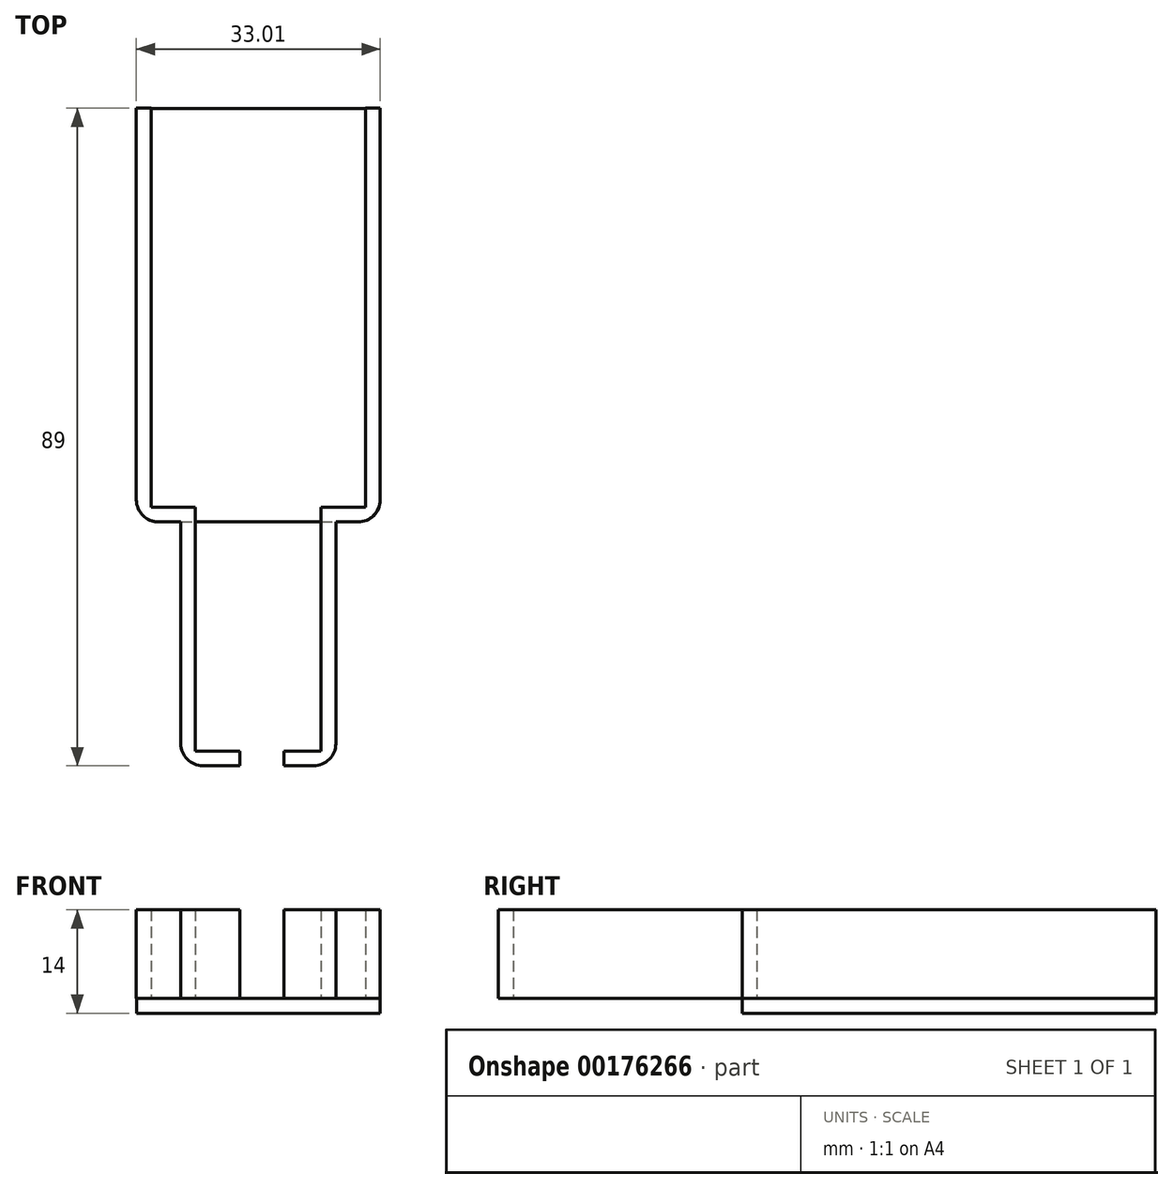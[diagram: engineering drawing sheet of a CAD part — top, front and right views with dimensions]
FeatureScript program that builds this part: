
annotation { "Feature Type Name" : "Feature", "Feature Type Description" : "" }
export const myFeature = defineFeature(function(context is Context, id is Id, definition is map)
    precondition{}
    {
        {
            var Q0;
            Q0=qCreatedBy(makeId("Top.planeOp"),FACE);
            var sketch = newSketch(context, id + "F0", { "sketchPlane" : qUnion([Q0])});
            skLineSegment(sketch, "E0.left", {"start": v(-20.44, 45.13) * mm, "end": v(-20.44, -8.87) * mm});
            skLineSegment(sketch, "E0.right", {"start": v(10.56, 45.13) * mm, "end": v(10.56, -8.87) * mm});
            skLineSegment(sketch, "E1.top", {"start": v(-14.44, -43.87) * mm, "end": v(-6.44, -43.87) * mm});
            skLineSegment(sketch, "E1.left", {"start": v(-14.44, -10.87) * mm, "end": v(-14.44, -43.87) * mm});
            skLineSegment(sketch, "E1.right", {"start": v(6.56, -10.87) * mm, "end": v(6.56, -43.87) * mm});
            skLineSegment(sketch, "E2", {"start": v(-6.44, -43.87) * mm, "end": v(-6.44, -43.87) * mm});
            skLineSegment(sketch, "E3", {"start": v(-0.44, -43.87) * mm, "end": v(-0.44, -43.87) * mm});
            skLineSegment(sketch, "E4.trimOffspring", {"start": v(-0.44, -43.87) * mm, "end": v(6.56, -43.87) * mm});
            skLineSegment(sketch, "E5.0", {"start": v(-0.44, -41.87) * mm, "end": v(4.56, -41.87) * mm});
            skLineSegment(sketch, "E6.0", {"start": v(4.56, -8.87) * mm, "end": v(4.56, -41.87) * mm});
            skLineSegment(sketch, "E7.0", {"start": v(-12.44, -8.87) * mm, "end": v(-12.44, -41.87) * mm});
            skLineSegment(sketch, "E8.0", {"start": v(-12.44, -41.87) * mm, "end": v(-6.44, -41.87) * mm});
            skLineSegment(sketch, "E9.0", {"start": v(12.56, 45.13) * mm, "end": v(12.56, -8.87) * mm});
            skLineSegment(sketch, "E10", {"start": v(-6.44, -41.87) * mm, "end": v(-6.44, -43.87) * mm});
            skLineSegment(sketch, "E11", {"start": v(-0.44, -41.87) * mm, "end": v(-0.44, -43.87) * mm});
            skLineSegment(sketch, "E12", {"start": v(-20.44, 45.13) * mm, "end": v(-18.44, 45.13) * mm});
            skLineSegment(sketch, "E13", {"start": v(-20.44, -8.87) * mm, "end": v(-20.44, -10.87) * mm});
            skLineSegment(sketch, "E14", {"start": v(-20.44, -10.87) * mm, "end": v(-14.44, -10.87) * mm});
            skPoint(sketch, "E15.end.orphan", {"position": v(-18.44, -8.87) * mm});
            skLineSegment(sketch, "E16", {"start": v(-18.44, 45.13) * mm, "end": v(-18.44, -8.87) * mm});
            skLineSegment(sketch, "E17", {"start": v(12.56, -8.87) * mm, "end": v(12.56, -10.87) * mm});
            skLineSegment(sketch, "E18", {"start": v(12.56, -10.87) * mm, "end": v(6.56, -10.87) * mm});
            skLineSegment(sketch, "E19", {"start": v(-12.44, -8.87) * mm, "end": v(-18.44, -8.87) * mm});
            skLineSegment(sketch, "E20", {"start": v(4.56, -8.87) * mm, "end": v(10.56, -8.87) * mm});
            skLineSegment(sketch, "E21", {"start": v(10.56, 45.13) * mm, "end": v(12.56, 45.13) * mm});
            skSolve(sketch);
        }
        {
            var Q0;
            Q0=makeQuery(id+"F0.imprint","IMPRINT",FACE,{"disambiguationData":[TD([[makeQuery(id+"F0.imprint","IMPRINT",EDGE,{"derivedFrom":sQuery(id+"F0.wireOp",EDGE,"E0.left")}),1.0]])]});
            var Q1;
            Q1=makeQuery(id+"F0.imprint","IMPRINT",FACE,{"disambiguationData":[TD([[makeQuery(id+"F0.imprint","IMPRINT",EDGE,{"derivedFrom":sQuery(id+"F0.wireOp",EDGE,"E0.right")}),1.0]])]});
            var Q2;
            {var subQ0=sQuery(id+"F0.wireOp",EDGE,"E3");Q2=makeQuery(id+"F0.imprint","IMPRINT",FACE,{"disambiguationData":[TD([[makeQuery(id+"F0.imprint","IMPRINT",EDGE,{"derivedFrom":subQ0}),-1.0]])]});}
            extrude(context, id + "F1", {"entities" : qUnion([Q0, Q1, Q2]), "depth" : 12 * mm});
        }
        {
            var Q0;
            Q0=qCreatedBy(makeId("Top.planeOp"),FACE);
            var sketch = newSketch(context, id + "F2", { "sketchPlane" : qUnion([Q0])});
            skLineSegment(sketch, "E22.bottom", {"start": v(-20.43, 45.12) * mm, "end": v(12.57, 45.12) * mm});
            skLineSegment(sketch, "E22.top", {"start": v(-20.43, -10.88) * mm, "end": v(12.57, -10.88) * mm});
            skLineSegment(sketch, "E22.left", {"start": v(-20.43, 45.12) * mm, "end": v(-20.43, -10.88) * mm});
            skLineSegment(sketch, "E22.right", {"start": v(12.57, 45.12) * mm, "end": v(12.57, -10.88) * mm});
            skLineSegment(sketch, "E23.bottom", {"start": v(-14.44, -10.88) * mm, "end": v(6.57, -10.88) * mm});
            skLineSegment(sketch, "E23.top", {"start": v(-14.44, -43.86) * mm, "end": v(6.57, -43.86) * mm});
            skLineSegment(sketch, "E23.left", {"start": v(-14.44, -10.88) * mm, "end": v(-14.44, -43.86) * mm});
            skLineSegment(sketch, "E23.right", {"start": v(6.57, -10.88) * mm, "end": v(6.57, -43.86) * mm});
            skSolve(sketch);
        }
        {
            var Q0;
            Q0=makeQuery(id+"F2.imprint","IMPRINT",FACE,{"disambiguationData":[TD([[makeQuery(id+"F2.imprint","IMPRINT",EDGE,{"derivedFrom":sQuery(id+"F2.wireOp",EDGE,"E22.bottom")}),-1.0]])]});
            var Q1;
            Q1=makeQuery(id+"F2.imprint","IMPRINT",FACE,{"disambiguationData":[TD([[makeQuery(id+"F2.imprint","IMPRINT",EDGE,{"derivedFrom":sQuery(id+"F2.wireOp",EDGE,"E23.bottom")}),-1.0]])]});
            var Q2;
            Q2=sQuery(id+"F2.wireOp",EDGE,"E23.right");
            var Q3;
            Q3=sQuery(id+"F2.wireOp",EDGE,"E22.bottom");
            var Q4;
            Q4=sQuery(id+"F2.wireOp",EDGE,"E22.top");
            var Q5;
            Q5=sQuery(id+"F2.wireOp",EDGE,"E22.left");
            var Q6;
            Q6=sQuery(id+"F2.wireOp",EDGE,"E22.right");
            var Q7;
            Q7=sQuery(id+"F2.wireOp",EDGE,"E23.bottom");
            var Q8;
            Q8=sQuery(id+"F2.wireOp",EDGE,"E23.top");
            var Q9;
            Q9=sQuery(id+"F2.wireOp",EDGE,"E23.left");
            extrude(context, id + "F3", {"entities" : qUnion([Q0, Q1]), "surfaceEntities" : qUnion([Q2, Q3, Q4, Q5, Q6, Q7, Q8, Q9]), "oppositeDirection" : true, "depth" : 2 * mm});
        }
        {
            var Q0;
            Q0=makeQuery(id+"F1.opExtrude","SWEPT_EDGE",EDGE,{"disambiguationData":[OSD([sQuery(id+"F0.wireOp",EDGE,"E13"),sQuery(id+"F0.wireOp",EDGE,"E14")])]});
            var Q1;
            Q1=makeQuery(id+"F1.opExtrude","SWEPT_EDGE",EDGE,{"disambiguationData":[OSD([sQuery(id+"F0.wireOp",EDGE,"E1.top"),sQuery(id+"F0.wireOp",EDGE,"E1.left")])]});
            var Q2;
            Q2=makeQuery(id+"F1.opExtrude","SWEPT_EDGE",EDGE,{"disambiguationData":[OSD([sQuery(id+"F0.wireOp",EDGE,"E1.right"),sQuery(id+"F0.wireOp",EDGE,"E4.trimOffspring")])]});
            var Q3;
            Q3=makeQuery(id+"F1.opExtrude","SWEPT_EDGE",EDGE,{"disambiguationData":[OSD([sQuery(id+"F0.wireOp",EDGE,"E17"),sQuery(id+"F0.wireOp",EDGE,"E18")])]});
            var Q4;
            Q4=makeQuery(id+"F3.opExtrude","SWEPT_EDGE",EDGE,{"disambiguationData":[OSD([sQuery(id+"F2.wireOp",EDGE,"E23.top"),sQuery(id+"F2.wireOp",EDGE,"E23.left")])]});
            var Q5;
            Q5=makeQuery(id+"F3.opExtrude","SWEPT_EDGE",EDGE,{"disambiguationData":[OSD([sQuery(id+"F2.wireOp",EDGE,"E23.top"),sQuery(id+"F2.wireOp",EDGE,"E23.right")])]});
            var Q6;
            Q6=makeQuery(id+"F3.opExtrude","SWEPT_EDGE",EDGE,{"disambiguationData":[OSD([sQuery(id+"F2.wireOp",EDGE,"E22.top"),sQuery(id+"F2.wireOp",EDGE,"E22.right")])]});
            var Q7;
            Q7=makeQuery(id+"F3.opExtrude","SWEPT_EDGE",EDGE,{"disambiguationData":[OSD([sQuery(id+"F2.wireOp",EDGE,"E22.top"),sQuery(id+"F2.wireOp",EDGE,"E22.left")])]});
            fillet(context, id + "F4", {"entities" : qUnion([Q0, Q1, Q2, Q3, Q4, Q5, Q6, Q7]), "radius" : 3 * mm, "tangentPropagation" : true, "allowEdgeOverflow" : false});
        }
    });
